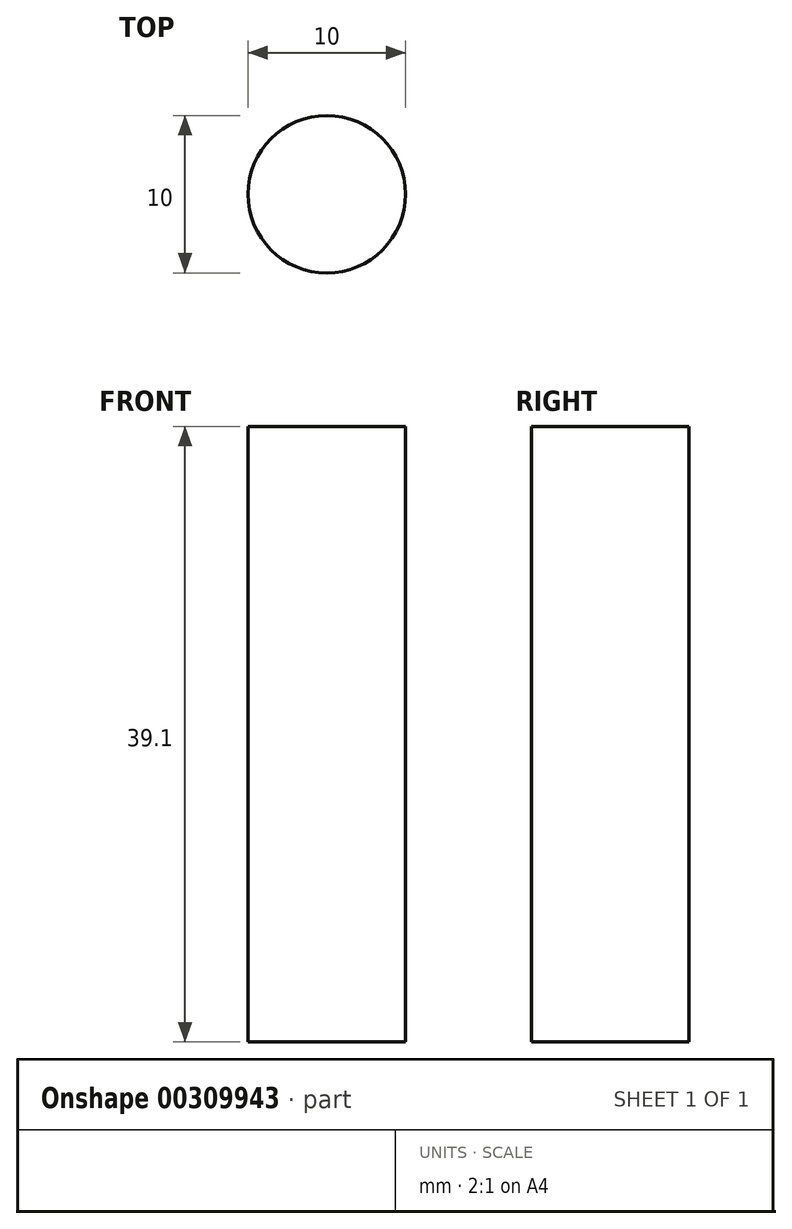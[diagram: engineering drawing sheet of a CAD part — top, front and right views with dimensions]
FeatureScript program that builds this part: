
annotation { "Feature Type Name" : "Feature", "Feature Type Description" : "" }
export const myFeature = defineFeature(function(context is Context, id is Id, definition is map)
    precondition{}
    {
        {
            var Q0;
            Q0=qCreatedBy(makeId("Top.planeOp"),FACE);
            var sketch = newSketch(context, id + "F0", { "sketchPlane" : qUnion([Q0])});
            skCircle(sketch, "E0", {"center": v(0, 0) * mm, "radius": 5 * mm});
            skSolve(sketch);
        }
        {
            var Q0;
            Q0=makeQuery(id+"F0.imprint","IMPRINT",FACE,{"disambiguationData":[TD([[makeQuery(id+"F0.imprint","IMPRINT",EDGE,{"derivedFrom":sQuery(id+"F0.wireOp",EDGE,"E0")}),1.0]])]});
            extrude(context, id + "F1", {"entities" : qUnion([Q0]), "depth" : 39.1 * mm, "offsetDistance" : 25 * mm});
        }
    });
